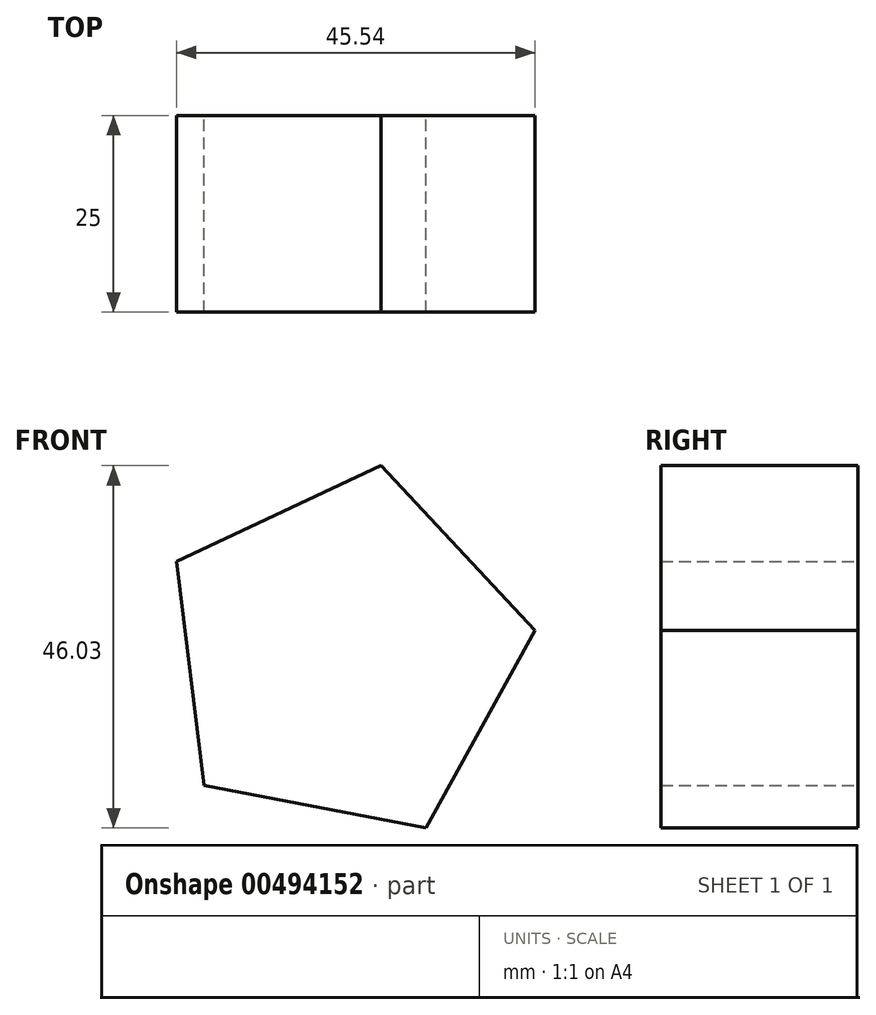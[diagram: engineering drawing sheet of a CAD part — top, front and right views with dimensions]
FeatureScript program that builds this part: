
annotation { "Feature Type Name" : "Feature", "Feature Type Description" : "" }
export const myFeature = defineFeature(function(context is Context, id is Id, definition is map)
    precondition{}
    {
        {
            var Q0;
            Q0=qCreatedBy(makeId("Front.planeOp"),FACE);
            var sketch = newSketch(context, id + "F0", { "sketchPlane" : qUnion([Q0])});
            skCircle(sketch, "E0.cCircle", {"center": v(-7.75, 9.61) * mm, "radius": 24.39 * mm, "construction": true});
            skLineSegment(sketch, "E0.0", {"start": v(2.58, -12.48) * mm, "end": v(-25.56, -7.04) * mm});
            skLineSegment(sketch, "E0.1", {"start": v(-25.56, -7.04) * mm, "end": v(-29.09, 21.41) * mm});
            skLineSegment(sketch, "E0.2", {"start": v(-29.09, 21.41) * mm, "end": v(-3.12, 33.55) * mm});
            skLineSegment(sketch, "E0.3", {"start": v(-3.12, 33.55) * mm, "end": v(16.45, 12.6) * mm});
            skLineSegment(sketch, "E0.4", {"start": v(16.45, 12.6) * mm, "end": v(2.58, -12.48) * mm});
            skSolve(sketch);
        }
        {
            var Q0;
            Q0=makeQuery(id+"F0.imprint","IMPRINT",FACE,{"disambiguationData":[TD([[makeQuery(id+"F0.imprint","IMPRINT",EDGE,{"derivedFrom":sQuery(id+"F0.wireOp",EDGE,"E0.0")}),-1.0]])]});
            extrude(context, id + "F1", {"entities" : qUnion([Q0]), "depth" : 25 * mm});
        }
    });
